# Revit family: KDW010001
name_source: partatom
category: Plumbing Fixtures
revit_build: Autodesk Revit 2015 (Build: 20140606_1530(x64)
units: mm (PartAtom-declared; Revit-internal decimal feet)

## types (1)
- KDW010001
    Accessory = Yes
    BIMobject category = Bath & Spas
    Brand url = http://www.kaldewei.com
    Chrome = Chrome
    Color = https://www.kaldewei.co.uk
    ColourOptions = https://www.kaldewei.co.uk
    ConnectingDimensions = EN 232
    Design country = Germany
    DrainSize = 52 mm
    Durability = https://www.kaldewei.de
    Edition number = 1
    Features = https://www.kaldewei.co.uk
    Finish = https://www.kaldewei.co.uk
    Finition = Kaldewei
    HasGrabHandles = https://www.kaldewei.co.uk
    IFC Classification = Furnishing Element
    IfcExportAs = BATH
    IfcExportType = IfcSanitaryTerminalType
    IntegralAccessories = https://www.kaldewei.co.uk
    Manufacturer = Kaldewei
    Manufacturer country = Germany
    ManufacturerCountry = GERMANY
    ManufacturerName = KALDEWEI
    ManufacturerURL = https://www.kaldewei.com
    Material = steel enamel
    Material main = Steel
    Material secondary = Enamel
    Model = CLASSIC DUO
    NBS Reference Code = 35-06-08
    NBS Reference Description = Baths
    Name = CLASSIC DUO
    Nominal height = 700 cm
    Nominal width = 1600 cm
    NominalDepth = 430
    NominalLength = 1600
    ObjectName = CLASSIC DUO 700x1600x430
    ObjectNorm = EN 14516EU DECLARATION OF PERFORMANCE(https://www.kaldewei.de
    ObjectPicture = https://www.kaldewei.co.uk
    ObjectURL = https://www.kaldewei.co.uk
    Polantis code = KDW010001
    Product Guid = 3962ff3f-65f5-4d9d-ab9d-4609452f1e34
    Product SKU = 103
    Product certification = https://www.kaldewei.co.uk
    Product data url = http://bimobject.com
    Product family = CLASSIC DUO
    Product group = Bathtub
    Product url = https://www.kaldewei.co.uk
    ProductInformation = Model No.103: The CLASSIC DUO baths radiate timeless and harmonious design. As reduced as necessary, as comfortable as possible. The inner shape of these baths extends an invitation to two people to take a seat and enjoy the comfort of two identical backrests.
    QR code = http://bimobject.com
    Revision = 1
    SerialNumber = 103
    Shape = Rectangular baths
    Size = 700x1600x430
    SupportFrame = https://www.kaldewei.co.uk
    Sustainability = https://kaldewei-fa.secure.footprint.net
    Technical description = https://www.kaldewei.co.uk
    TechnicalDataURL = https://kaldewei.typo-live.web-factory.de
    Type Comments = CLASSIC DUO 103 700x1600x430
    UNSPSC Code = 30181501
    UNSPSCCode = 30181500
    UNSPSCNames = Sanitary ware
    URL = https://www.kaldewei.co.uk
    Uniclass 1.4 Code = L7211
    Uniclass 1.4 Description = Baths
    Uniclass 2.0 Code = PR-35-06-08
    Uniclass 2.0 Description = Baths
    Uniclass 2015 = Pr_40_20_06_08
    Version = 5
    VolumeToOverflowMaximum = 95
    WarrantyDurationParts = 30
    WarrantyDurationUnit = Year
    WarrantyStartDate = https://www.kaldewei.co.uk
    WaterSupplyOverflowAndWasteHolesOverflow = 52 mm
    WaterSupplyOverflowAndWasteHolesWaste = 52 mm
    Weight = 44
    Weight Net (Kg) = 44

## geometry (parser evidence)
native form markers: Sweep x5
no freeform markers — native parametric forms only
